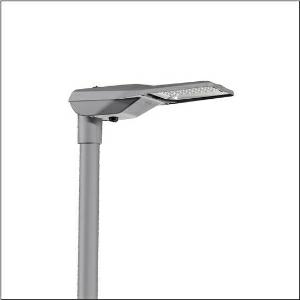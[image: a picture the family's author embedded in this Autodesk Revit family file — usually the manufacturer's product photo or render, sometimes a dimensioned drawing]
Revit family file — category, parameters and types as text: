
# Revit family: streetlight_sl_21_mini___st0_8a_5xe2c43t08gb_5b97
name_source: partatom
category: Lighting Fixtures
units: mm (PartAtom-declared; Revit-internal decimal feet)

## family parameters
Cut with Voids When Loaded = No
Host = Face
Light Source = No
Part Type = Normal
Room Calculation Point = No
Round Connector Dimension = Use Diameter
Shared = No

## types (1)
- --- (1 x LED, 6180 lm, 40.4 W, 4000K)
    Apparent Load = 40 VA
    CIE Flux Codes = 38 75 97 100 100
    Color Rendering = 70
    Color Temperature = 4000K
    Default Elevation = 1800 mm
    Description = Streetlight SL 21 mini, mast luminaire, primary light control with lens, of PMMA, primary optical cover: cover, of toughened safety glass, transparent, light distribution: ST0.8a, light emission: direct distribution, primary light characteristic: asymmetric, installation type: side-entry, post-top, LED, High Power LED, rated luminous flux: 6.180lm, luminous efficacy: 153lm/W, light colour: 740, colour temperature: 4000K, control gear: D4i, control: overheat protection, constant luminous flux control, time-dependent luminous flux control, flexible luminous flux parameterisation, pre-setting: logarithmic dimming characteristic, mains connection: 220..240V, AC, 50/60Hz, start of lifetime: 40W, end of service life: 41W, reduction: 19W, luminaire housing, of diecast aluminium, powder-coated, SITECO metallic grey (DB 702S), corrosivity category C5 high according to DIN EN ISO 12944, please order mast flange separately, inclination adjustable: 0°, 5°, 10°, 15°, sealing non-destructively replaceable, multi-level sealing system, length: 628mm, width: 235mm, height: 110mm, mast flange for spigot size: 42mm (side-entry): 5XC10008XM4, 60/48mm (side-entry/post-top): 5XC10108XM2, 76/60mm (side-entry/post-top): 5XC10108XM1, mounting height: 4..8m, Smart Interface below and above, protection rating (complete): IP66, insulation class (complete): insulation class II (safety insulation), certification: CE, ENEC, ENEC+, VDE, impact resistance: IK10, permissible operating ambient temperature for outdoor applications: -40..+50°C, standard-compliant lighting for roads and squares, packaging unit: 1 piece

Light Distribution: ST0.8a
    Height = 110 mm
    Lamp = 1 x LED
    Lamp Light Flux = 6180 lm
    Lamp Power = 40.4 W
    Lamp count = 1
    Length = 625 mm
    Luminous efficacy = 153 lm/W
    Manufacturer = Siteco
    ModVariant = No
    Model = 5XE2C43T08GB
    Number of Poles = 1
    OnlyDefault = Yes
    Power Factor = 1
    Product Name = Streetlight SL 21 mini | ST0.8a
    Product group = mast luminaire | pylon top
    ProductGroupID = 6100
    Protection Class = Protection class II
    Protection Degree = IP 66
    RLX_Detail_Level = 1
    RLX_Emergency_Light_Flux = 0 lm
    RLX_Emergency_Type = 0
    RLX_Emergency_Type_DB = No
    RlxData = <blob elided: 26377 chars, md5=4ecf592c>
    Socket = socket
    Standby Power = 0 W
    System Light Flux = 6180 lm
    System Power = 40 W
    Type Comments = factory setting: luminous flux: 100 % | dim-lin: 254 | 812 mA
    Type Image = l_1003514.jpg
    URL = http://relux.com
    VarID = @adj_182843
    Voltage = 0 V
    Weight = 0.00 kg
    Width = 234 mm

## geometry (parser evidence)
native form markers: Blend x4, Sweep x12
no freeform markers — native parametric forms only
